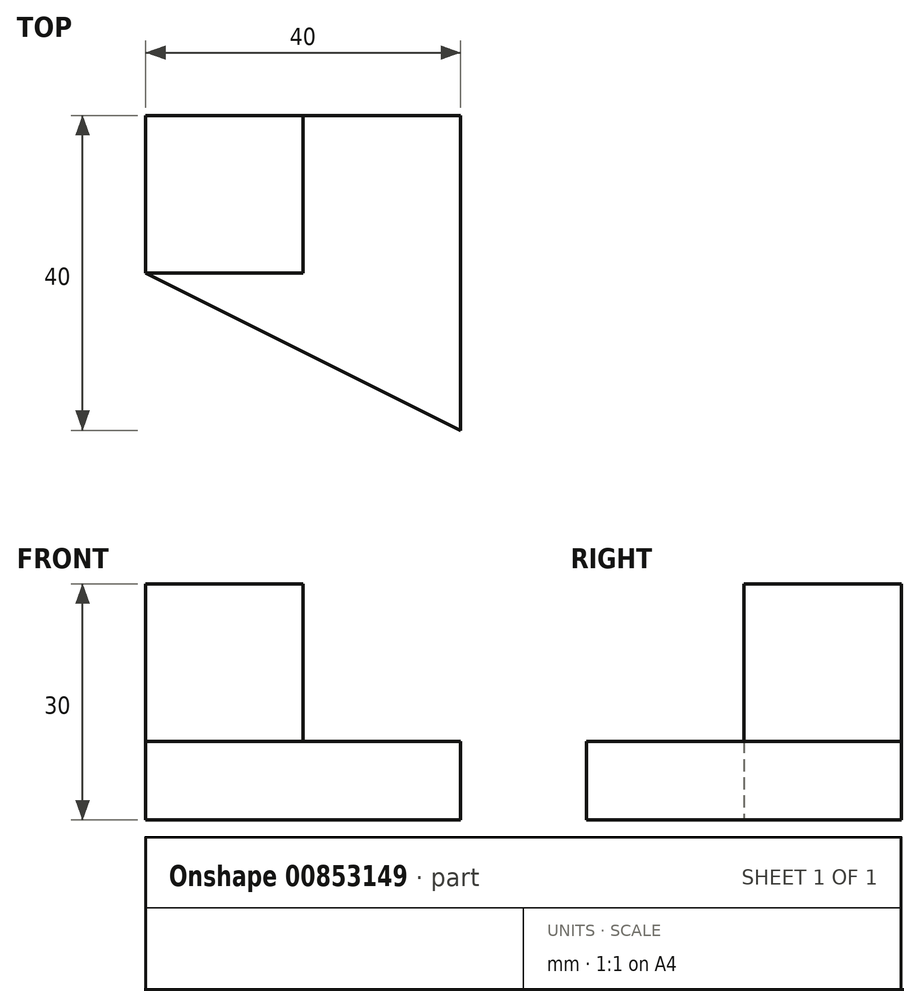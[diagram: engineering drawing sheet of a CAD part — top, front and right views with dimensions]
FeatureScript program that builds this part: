
annotation { "Feature Type Name" : "Feature", "Feature Type Description" : "" }
export const myFeature = defineFeature(function(context is Context, id is Id, definition is map)
    precondition{}
    {
        {
            var Q0;
            Q0=qCreatedBy(makeId("Top.planeOp"),FACE);
            var sketch = newSketch(context, id + "F0", { "sketchPlane" : qUnion([Q0])});
            skLineSegment(sketch, "E0", {"start": v(-30, 0) * mm, "end": v(-30, 20) * mm});
            skLineSegment(sketch, "E1", {"start": v(-30, 20) * mm, "end": v(10, 20) * mm});
            skLineSegment(sketch, "E2", {"start": v(10, 20) * mm, "end": v(10, -20) * mm});
            skLineSegment(sketch, "E3", {"start": v(10, -20) * mm, "end": v(-30, 0) * mm});
            skLineSegment(sketch, "E4", {"start": v(-30, 0) * mm, "end": v(-10, 0) * mm});
            skLineSegment(sketch, "E5", {"start": v(-10, 0) * mm, "end": v(-10, 20) * mm});
            skSolve(sketch);
        }
        {
            var Q0;
            {var subQ0=sQuery(id+"F0.wireOp",EDGE,"E2");Q0=makeQuery(id+"F0.imprint","IMPRINT",FACE,{"disambiguationData":[TD([[makeQuery(id+"F0.imprint","IMPRINT",EDGE,{"derivedFrom":subQ0}),-1.0]])]});}
            extrude(context, id + "F1", {"entities" : qUnion([Q0]), "depth" : 10 * mm, "offsetDistance" : 25 * mm});
        }
        {
            var Q0;
            {var subQ0=sQuery(id+"F0.wireOp",EDGE,"E0");Q0=makeQuery(id+"F0.imprint","IMPRINT",FACE,{"disambiguationData":[TD([[makeQuery(id+"F0.imprint","IMPRINT",EDGE,{"derivedFrom":subQ0}),-1.0]])]});}
            extrude(context, id + "F2", {"entities" : qUnion([Q0]), "operationType" : NewBodyOperationType.ADD, "depth" : 30 * mm, "offsetDistance" : 25 * mm});
        }
    });
